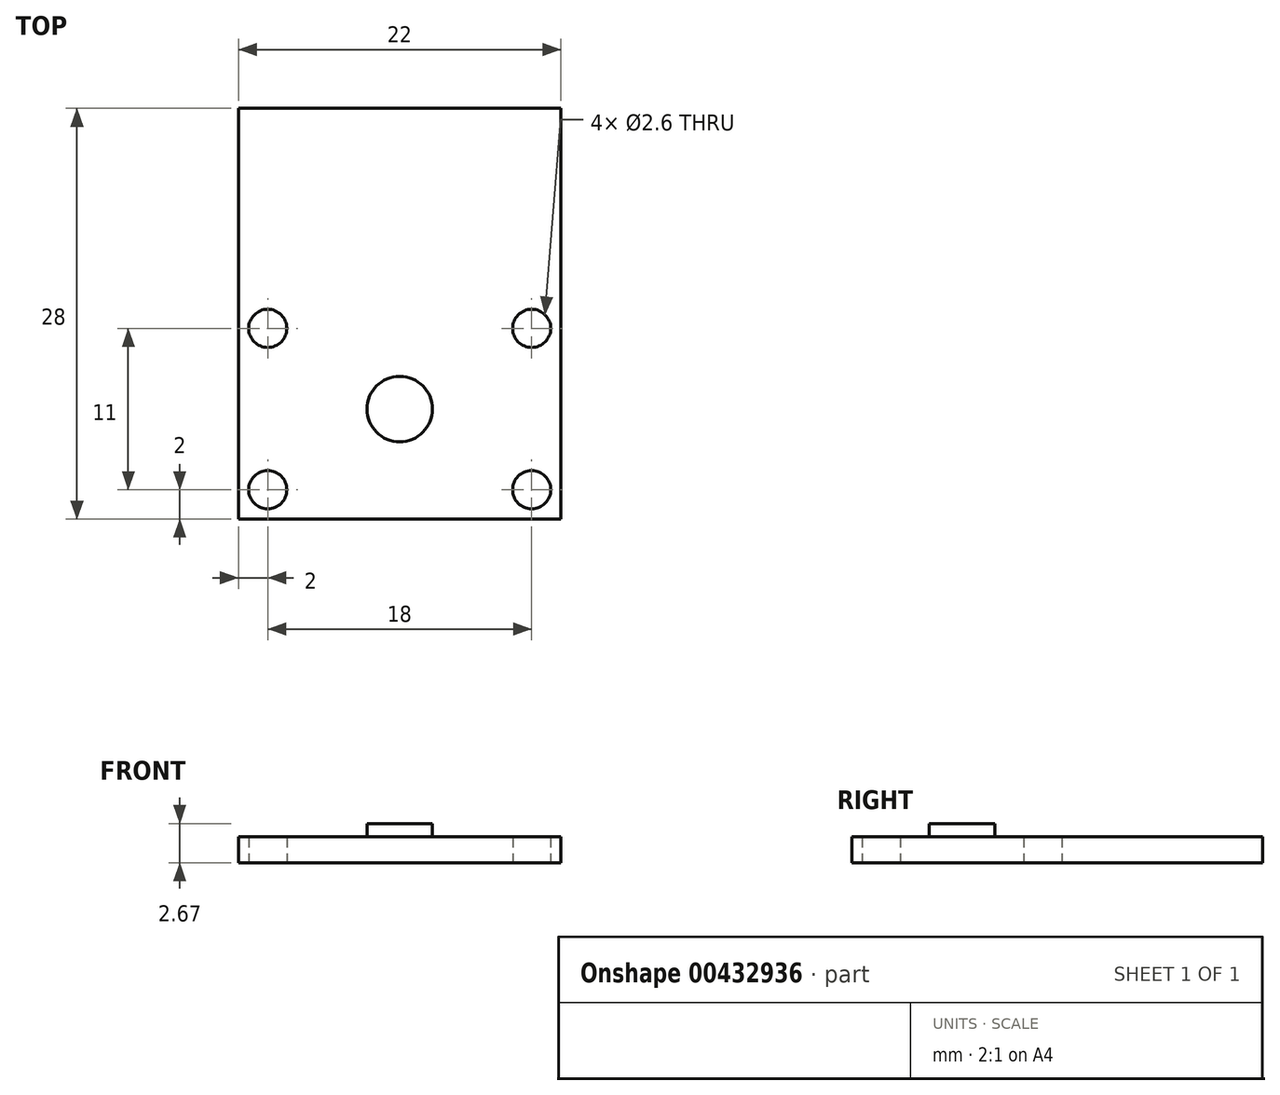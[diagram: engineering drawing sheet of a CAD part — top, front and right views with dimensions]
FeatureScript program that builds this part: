
annotation { "Feature Type Name" : "Feature", "Feature Type Description" : "" }
export const myFeature = defineFeature(function(context is Context, id is Id, definition is map)
    precondition{}
    {
        {
            var Q0;
            Q0=qCreatedBy(makeId("Top.planeOp"),FACE);
            var sketch = newSketch(context, id + "F0", { "sketchPlane" : qUnion([Q0])});
            skLineSegment(sketch, "E0.bottom", {"start": v(-11, 20.5) * mm, "end": v(11, 20.5) * mm});
            skLineSegment(sketch, "E0.top", {"start": v(-11, -7.5) * mm, "end": v(11, -7.5) * mm});
            skLineSegment(sketch, "E0.left", {"start": v(-11, 20.5) * mm, "end": v(-11, -7.5) * mm});
            skLineSegment(sketch, "E0.right", {"start": v(11, 20.5) * mm, "end": v(11, -7.5) * mm});
            skCircle(sketch, "E1", {"center": v(-9, -5.5) * mm, "radius": 1.3 * mm});
            skLineSegment(sketch, "E2", {"start": v(0, 0) * mm, "end": v(-16.7, 0) * mm, "construction": true});
            skLineSegment(sketch, "E3", {"start": v(0, 0) * mm, "end": v(0, -8.66) * mm, "construction": true});
            skPoint(sketch, "E3.endSnap0", {"position": v(0, -7.5) * mm});
            skCircle(sketch, "E4.MirrorC", {"center": v(9, -5.5) * mm, "radius": 1.3 * mm});
            skCircle(sketch, "E5.MirrorC", {"center": v(9, 5.5) * mm, "radius": 1.3 * mm});
            skCircle(sketch, "E6.MirrorC", {"center": v(-9, 5.5) * mm, "radius": 1.3 * mm});
            skPoint(sketch, "E7", {"position": v(0, 0) * mm});
            skSolve(sketch);
        }
        {
            var Q0;
            Q0=qSketchRegion(id+"F0",true);
            extrude(context, id + "F1", {"entities" : qUnion([Q0]), "depth" : 1.78 * mm});
        }
        {
            var Q0;
            Q0=makeQuery(id+"F1.opExtrude","CAP_FACE",FACE,{"disambiguationData":[OSD([sQuery(id+"F0.wireOp",EDGE,"E0.bottom"),sQuery(id+"F0.wireOp",EDGE,"E0.top"),sQuery(id+"F0.wireOp",EDGE,"E0.left"),sQuery(id+"F0.wireOp",EDGE,"E0.right"),sQuery(id+"F0.wireOp",EDGE,"E1"),sQuery(id+"F0.wireOp",EDGE,"E4.MirrorC"),sQuery(id+"F0.wireOp",EDGE,"E5.MirrorC"),sQuery(id+"F0.wireOp",EDGE,"E6.MirrorC")])],"isStart":false});
            var sketch = newSketch(context, id + "F2", { "sketchPlane" : qUnion([Q0])});
            skCircle(sketch, "E8", {"center": v(0, 0) * mm, "radius": 2.23 * mm});
            skSolve(sketch);
        }
        {
            var Q0;
            Q0=qSketchRegion(id+"F2",true);
            extrude(context, id + "F3", {"entities" : qUnion([Q0]), "operationType" : NewBodyOperationType.ADD, "depth" : 0.89 * mm});
        }
    });
